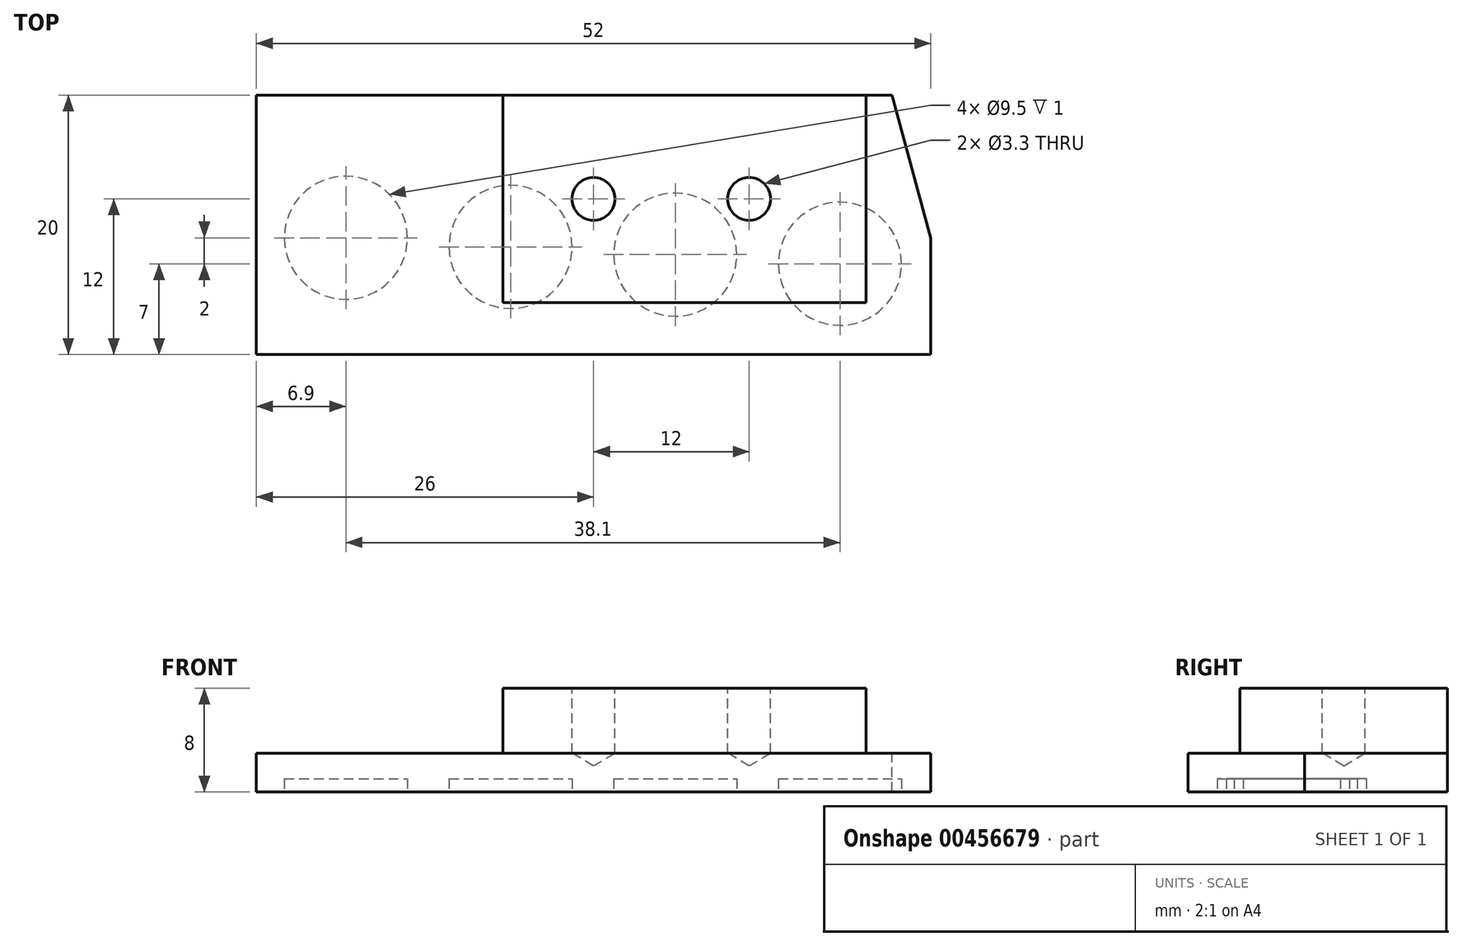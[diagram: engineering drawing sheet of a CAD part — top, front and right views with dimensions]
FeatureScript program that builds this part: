
annotation { "Feature Type Name" : "Feature", "Feature Type Description" : "" }
export const myFeature = defineFeature(function(context is Context, id is Id, definition is map)
    precondition{}
    {
        {
            var Q0;
            Q0=qCreatedBy(makeId("Top.planeOp"),FACE);
            var sketch = newSketch(context, id + "F0", { "sketchPlane" : qUnion([Q0])});
            skLineSegment(sketch, "E0", {"start": v(-26, 10) * mm, "end": v(23, 10) * mm});
            skLineSegment(sketch, "E1", {"start": v(-26, 10) * mm, "end": v(-26, -10) * mm});
            skLineSegment(sketch, "E2", {"start": v(-26, -10) * mm, "end": v(26, -10) * mm});
            skLineSegment(sketch, "E3", {"start": v(26, -10) * mm, "end": v(26, -1) * mm});
            skLineSegment(sketch, "E4", {"start": v(23, 10) * mm, "end": v(26, -1) * mm});
            skSolve(sketch);
        }
        {
            var Q0;
            Q0=makeQuery(id+"F0.imprint","IMPRINT",FACE,{"disambiguationData":[TD([[makeQuery(id+"F0.imprint","IMPRINT",EDGE,{"derivedFrom":sQuery(id+"F0.wireOp",EDGE,"E0")}),-1.0]])]});
            extrude(context, id + "F1", {"entities" : qUnion([Q0]), "oppositeDirection" : true, "depth" : 3 * mm, "offsetDistance" : 25 * mm});
        }
        {
            var Q0;
            Q0=makeQuery(id+"F1.opExtrude","CAP_FACE",FACE,{"disambiguationData":[OSD([sQuery(id+"F0.wireOp",EDGE,"E0"),sQuery(id+"F0.wireOp",EDGE,"E1"),sQuery(id+"F0.wireOp",EDGE,"E2"),sQuery(id+"F0.wireOp",EDGE,"E3"),sQuery(id+"F0.wireOp",EDGE,"E4")])],"isStart":false});
            var sketch = newSketch(context, id + "F2", { "sketchPlane" : qUnion([Q0])});
            skLineSegment(sketch, "E5", {"start": v(-19.1, 15.46) * mm, "end": v(-19.1, -23.34) * mm, "construction": true});
            skLineSegment(sketch, "E6", {"start": v(-6.4, 16.13) * mm, "end": v(-6.4, -12.73) * mm, "construction": true});
            skLineSegment(sketch, "E7", {"start": v(6.3, 13.93) * mm, "end": v(6.3, -24.02) * mm, "construction": true});
            skLineSegment(sketch, "E8", {"start": v(19, 29.34) * mm, "end": v(19, -23.34) * mm, "construction": true});
            skCircle(sketch, "E9", {"center": v(-19.1, 1) * mm, "radius": 4.75 * mm});
            skCircle(sketch, "E10", {"center": v(-6.4, 1.7) * mm, "radius": 4.75 * mm});
            skCircle(sketch, "E11", {"center": v(6.3, 2.3) * mm, "radius": 4.75 * mm});
            skCircle(sketch, "E12", {"center": v(19, 3) * mm, "radius": 4.75 * mm});
            skSolve(sketch);
        }
        {
            var Q0;
            Q0=makeQuery(id+"F2.imprint","IMPRINT",FACE,{"disambiguationData":[TD([[makeQuery(id+"F2.imprint","IMPRINT",EDGE,{"derivedFrom":sQuery(id+"F2.wireOp",EDGE,"E12")}),1.0]])]});
            var Q1;
            Q1=makeQuery(id+"F2.imprint","IMPRINT",FACE,{"disambiguationData":[TD([[makeQuery(id+"F2.imprint","IMPRINT",EDGE,{"derivedFrom":sQuery(id+"F2.wireOp",EDGE,"E11")}),1.0]])]});
            var Q2;
            Q2=makeQuery(id+"F2.imprint","IMPRINT",FACE,{"disambiguationData":[TD([[makeQuery(id+"F2.imprint","IMPRINT",EDGE,{"derivedFrom":sQuery(id+"F2.wireOp",EDGE,"E10")}),1.0]])]});
            var Q3;
            Q3=makeQuery(id+"F2.imprint","IMPRINT",FACE,{"disambiguationData":[TD([[makeQuery(id+"F2.imprint","IMPRINT",EDGE,{"derivedFrom":sQuery(id+"F2.wireOp",EDGE,"E9")}),1.0]])]});
            extrude(context, id + "F3", {"entities" : qUnion([Q0, Q1, Q2, Q3]), "operationType" : NewBodyOperationType.REMOVE, "oppositeDirection" : true, "depth" : 1 * mm, "offsetDistance" : 25 * mm});
        }
        {
            var Q0;
            Q0=makeQuery(id+"F1.opExtrude","CAP_FACE",FACE,{"disambiguationData":[OSD([sQuery(id+"F0.wireOp",EDGE,"E0"),sQuery(id+"F0.wireOp",EDGE,"E1"),sQuery(id+"F0.wireOp",EDGE,"E2"),sQuery(id+"F0.wireOp",EDGE,"E3"),sQuery(id+"F0.wireOp",EDGE,"E4")])],"isStart":true});
            var sketch = newSketch(context, id + "F4", { "sketchPlane" : qUnion([Q0])});
            skLineSegment(sketch, "E13.bottom", {"start": v(-7, 10) * mm, "end": v(21, 10) * mm});
            skLineSegment(sketch, "E13.top", {"start": v(-7, -6) * mm, "end": v(21, -6) * mm});
            skLineSegment(sketch, "E13.left", {"start": v(-7, 10) * mm, "end": v(-7, -6) * mm});
            skLineSegment(sketch, "E13.right", {"start": v(21, 10) * mm, "end": v(21, -6) * mm});
            skSolve(sketch);
        }
        {
            var Q0;
            Q0=makeQuery(id+"F4.imprint","IMPRINT",FACE,{"disambiguationData":[TD([[makeQuery(id+"F4.imprint","IMPRINT",EDGE,{"derivedFrom":sQuery(id+"F4.wireOp",EDGE,"E13.bottom")}),-1.0]])]});
            extrude(context, id + "F5", {"entities" : qUnion([Q0]), "operationType" : NewBodyOperationType.ADD, "depth" : 5 * mm, "offsetDistance" : 25 * mm});
        }
        {
            var Q0;
            Q0=makeQuery(id+"F5.opExtrude","CAP_FACE",FACE,{"disambiguationData":[OSD([sQuery(id+"F4.wireOp",EDGE,"E13.bottom"),sQuery(id+"F4.wireOp",EDGE,"E13.top"),sQuery(id+"F4.wireOp",EDGE,"E13.left"),sQuery(id+"F4.wireOp",EDGE,"E13.right")])],"isStart":false});
            var sketch = newSketch(context, id + "F6", { "sketchPlane" : qUnion([Q0])});
            skLineSegment(sketch, "E14", {"start": v(-53.05, 2) * mm, "end": v(58.18, 2) * mm, "construction": true});
            skLineSegment(sketch, "E15", {"start": v(0, 17.54) * mm, "end": v(0, -15.33) * mm, "construction": true});
            skLineSegment(sketch, "E16", {"start": v(12, 17.06) * mm, "end": v(12, -15.52) * mm, "construction": true});
            skCircle(sketch, "E17", {"center": v(0, 2) * mm, "radius": 2 * mm});
            skCircle(sketch, "E18", {"center": v(12, 2) * mm, "radius": 2 * mm});
            skSolve(sketch);
        }
        {
            var Q0;
            Q0=sQuery(id+"F6.wireOp",VERTEX,"E17.center");
            var Q1;
            Q1=sQuery(id+"F6.wireOp",VERTEX,"E18.center");
            var Q2;
            Q2=makeQuery(id+"F1.opExtrude","SWEPT_BODY",BODY,{"disambiguationData":[OSD([sQuery(id+"F0.wireOp",EDGE,"E0"),sQuery(id+"F0.wireOp",EDGE,"E1"),sQuery(id+"F0.wireOp",EDGE,"E2"),sQuery(id+"F0.wireOp",EDGE,"E3"),sQuery(id+"F0.wireOp",EDGE,"E4")])]});
            hole(context, id + "F7", {"style" : HoleStyle.SIMPLE, "endStyle" : HoleEndStyle.BLIND, "standardTappedOrClearance" : lookupTablePath({ "standard" : "ISO", "engagement" : "75%", "pitch" : "0.7 mm", "size" : "M4", "type" : "Tapped" }), "standardBlindInLast" : lookupTablePath({ "standard" : "ISO", "engagement" : "75%", "pitch" : "0.7 mm", "size" : "M4", "type" : "Tapped" }), "holeDiameter" : 3.3 * mm, "showTappedDepth" : true, "holeDepth" : 5 * mm, "tappedDepth" : 2.9 * mm, "tapClearance" : 3, "startFromSketch" : true, "locations" : qUnion([Q0, Q1]), "scope" : qUnion([Q2]), "majorDiameter" : 4 * mm});
        }
    });
